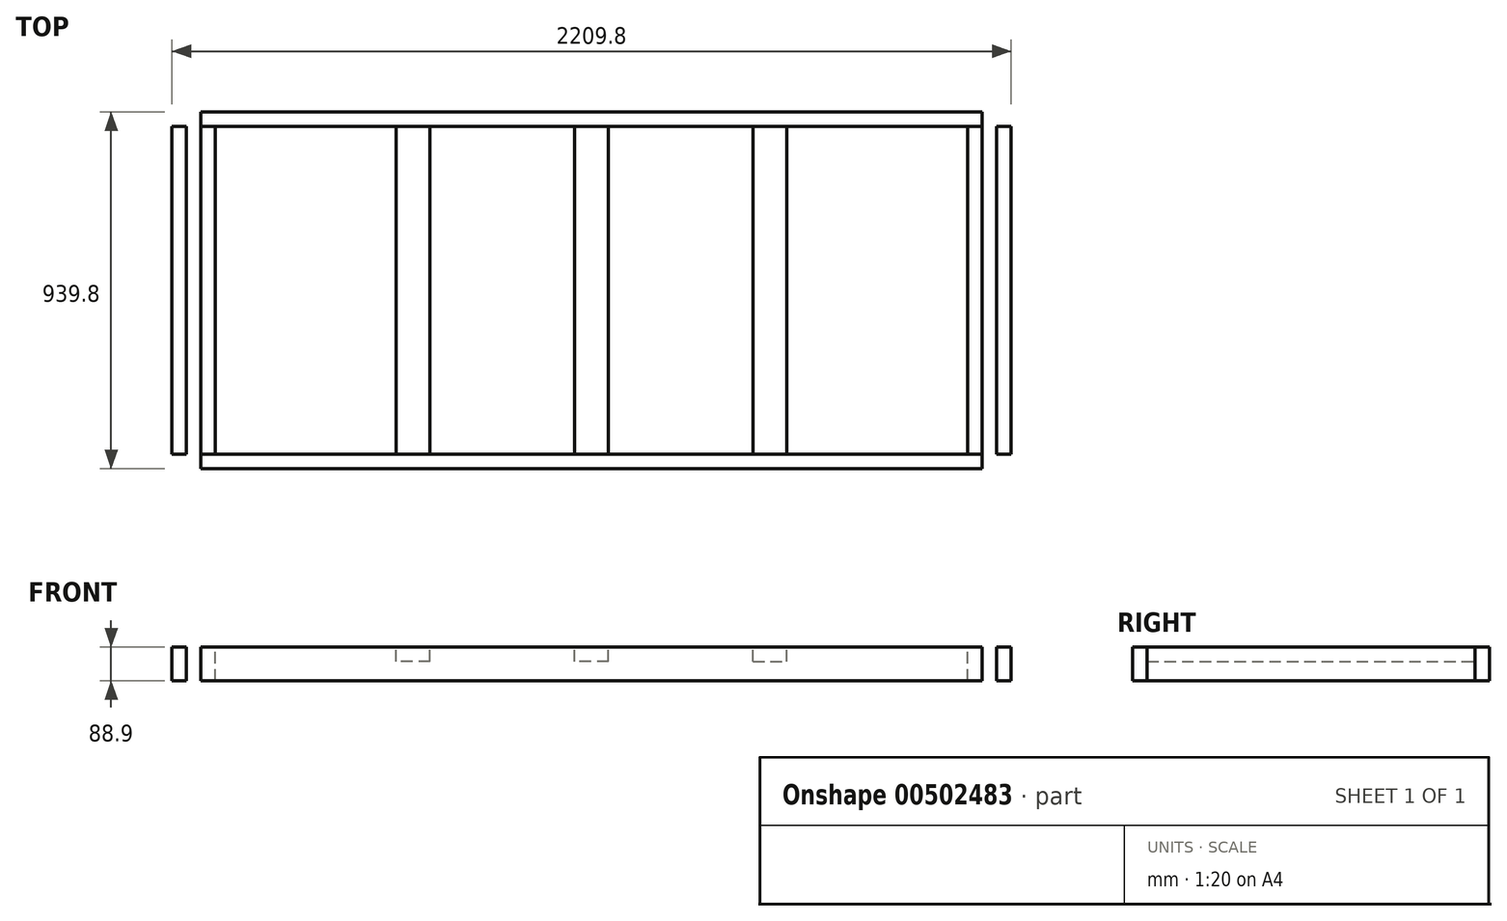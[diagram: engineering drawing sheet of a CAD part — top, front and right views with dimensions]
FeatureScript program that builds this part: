
annotation { "Feature Type Name" : "Feature", "Feature Type Description" : "" }
export const myFeature = defineFeature(function(context is Context, id is Id, definition is map)
    precondition{}
    {
        {
            var Q0;
            Q0=qCreatedBy(makeId("Top.planeOp"),FACE);
            var sketch = newSketch(context, id + "F0", { "sketchPlane" : qUnion([Q0])});
            skLineSegment(sketch, "E0.bottom", {"start": v(44.45, -431.8) * mm, "end": v(-44.45, -431.8) * mm});
            skLineSegment(sketch, "E0.top", {"start": v(44.45, 431.8) * mm, "end": v(-44.45, 431.8) * mm});
            skLineSegment(sketch, "E0.left", {"start": v(44.45, -431.8) * mm, "end": v(44.45, 431.8) * mm});
            skLineSegment(sketch, "E0.right", {"start": v(-44.45, -431.8) * mm, "end": v(-44.45, 431.8) * mm});
            skPoint(sketch, "E0.middle", {"position": v(0, 0) * mm});
            skSolve(sketch);
        }
        {
            var Q0;
            Q0=qCreatedBy(makeId("Top.planeOp"),FACE);
            var sketch = newSketch(context, id + "F1", { "sketchPlane" : qUnion([Q0])});
            skLineSegment(sketch, "E1", {"start": v(-832.76, 0) * mm, "end": v(832.76, 0) * mm, "construction": true});
            skSolve(sketch);
        }
        {
            var Q0;
            Q0=qCreatedBy(makeId("Top.planeOp"),FACE);
            var sketch = newSketch(context, id + "F2", { "sketchPlane" : qUnion([Q0])});
            skLineSegment(sketch, "E2.bottom", {"start": v(-425.45, -431.8) * mm, "end": v(-514.35, -431.8) * mm});
            skLineSegment(sketch, "E2.top", {"start": v(-425.45, 431.8) * mm, "end": v(-514.35, 431.8) * mm});
            skLineSegment(sketch, "E2.left", {"start": v(-425.45, -431.8) * mm, "end": v(-425.45, 431.8) * mm});
            skLineSegment(sketch, "E2.right", {"start": v(-514.35, -431.8) * mm, "end": v(-514.35, 431.8) * mm});
            skPoint(sketch, "E2.middle", {"position": v(-469.9, 0) * mm});
            skSolve(sketch);
        }
        {
            var Q0;
            Q0=qCreatedBy(makeId("Top.planeOp"),FACE);
            var sketch = newSketch(context, id + "F3", { "sketchPlane" : qUnion([Q0])});
            skLineSegment(sketch, "E3.bottom", {"start": v(425.45, 431.8) * mm, "end": v(514.35, 431.8) * mm});
            skLineSegment(sketch, "E3.top", {"start": v(425.45, -431.8) * mm, "end": v(514.35, -431.8) * mm});
            skLineSegment(sketch, "E3.left", {"start": v(425.45, 431.8) * mm, "end": v(425.45, -431.8) * mm});
            skLineSegment(sketch, "E3.right", {"start": v(514.35, 431.8) * mm, "end": v(514.35, -431.8) * mm});
            skPoint(sketch, "E3.middle", {"position": v(469.9, 0) * mm});
            skSolve(sketch);
        }
        {
            var Q0;
            Q0 = qSketchRegion(id + "F0", true);
            var Q1;
            Q1 = qSketchRegion(id + "F2", true);
            var Q2;
            Q2 = qSketchRegion(id + "F3", true);
            extrude(context, id + "F4", {"entities" : qUnion([Q0, Q1, Q2]), "oppositeDirection" : true, "depth" : 38.1 * mm});
        }
        {
            var Q0;
            Q0=qCreatedBy(makeId("Top.planeOp"),FACE);
            var sketch = newSketch(context, id + "F5", { "sketchPlane" : qUnion([Q0])});
            skLineSegment(sketch, "E4.bottom", {"start": v(-990.6, 431.8) * mm, "end": v(-1028.7, 431.8) * mm});
            skLineSegment(sketch, "E4.top", {"start": v(-990.6, -431.8) * mm, "end": v(-1028.7, -431.8) * mm});
            skLineSegment(sketch, "E4.left", {"start": v(-990.6, 431.8) * mm, "end": v(-990.6, -431.8) * mm});
            skLineSegment(sketch, "E4.right", {"start": v(-1028.7, 431.8) * mm, "end": v(-1028.7, -431.8) * mm});
            skPoint(sketch, "E4.middle", {"position": v(-1009.65, 0) * mm});
            skSolve(sketch);
        }
        {
            var Q0;
            Q0=qCreatedBy(makeId("Top.planeOp"),FACE);
            var sketch = newSketch(context, id + "F6", { "sketchPlane" : qUnion([Q0])});
            skLineSegment(sketch, "E5.bottom", {"start": v(-1066.8, 431.8) * mm, "end": v(-1104.9, 431.8) * mm});
            skLineSegment(sketch, "E5.top", {"start": v(-1066.8, -431.8) * mm, "end": v(-1104.9, -431.8) * mm});
            skLineSegment(sketch, "E5.left", {"start": v(-1066.8, 431.8) * mm, "end": v(-1066.8, -431.8) * mm});
            skLineSegment(sketch, "E5.right", {"start": v(-1104.9, 431.8) * mm, "end": v(-1104.9, -431.8) * mm});
            skPoint(sketch, "E5.middle", {"position": v(-1085.85, 0) * mm});
            skSolve(sketch);
        }
        {
            var Q0;
            Q0=qCreatedBy(makeId("Top.planeOp"),FACE);
            var sketch = newSketch(context, id + "F7", { "sketchPlane" : qUnion([Q0])});
            skLineSegment(sketch, "E6.bottom", {"start": v(990.6, 431.8) * mm, "end": v(1028.7, 431.8) * mm});
            skLineSegment(sketch, "E6.top", {"start": v(990.6, -431.8) * mm, "end": v(1028.7, -431.8) * mm});
            skLineSegment(sketch, "E6.left", {"start": v(990.6, 431.8) * mm, "end": v(990.6, -431.8) * mm});
            skLineSegment(sketch, "E6.right", {"start": v(1028.7, 431.8) * mm, "end": v(1028.7, -431.8) * mm});
            skPoint(sketch, "E6.middle", {"position": v(1009.65, 0) * mm});
            skSolve(sketch);
        }
        {
            var Q0;
            Q0=qCreatedBy(makeId("Top.planeOp"),FACE);
            var sketch = newSketch(context, id + "F8", { "sketchPlane" : qUnion([Q0])});
            skLineSegment(sketch, "E7.bottom", {"start": v(1066.8, 431.8) * mm, "end": v(1104.9, 431.8) * mm});
            skLineSegment(sketch, "E7.top", {"start": v(1066.8, -431.8) * mm, "end": v(1104.9, -431.8) * mm});
            skLineSegment(sketch, "E7.left", {"start": v(1066.8, 431.8) * mm, "end": v(1066.8, -431.8) * mm});
            skLineSegment(sketch, "E7.right", {"start": v(1104.9, 431.8) * mm, "end": v(1104.9, -431.8) * mm});
            skPoint(sketch, "E7.middle", {"position": v(1085.85, 0) * mm});
            skSolve(sketch);
        }
        {
            var Q0;
            Q0=qCreatedBy(makeId("Top.planeOp"),FACE);
            var sketch = newSketch(context, id + "F9", { "sketchPlane" : qUnion([Q0])});
            skLineSegment(sketch, "E8.bottom", {"start": v(-1028.7, 431.8) * mm, "end": v(1028.7, 431.8) * mm});
            skLineSegment(sketch, "E8.top", {"start": v(-1028.7, 469.9) * mm, "end": v(1028.7, 469.9) * mm});
            skLineSegment(sketch, "E8.left", {"start": v(-1028.7, 431.8) * mm, "end": v(-1028.7, 469.9) * mm});
            skLineSegment(sketch, "E8.right", {"start": v(1028.7, 431.8) * mm, "end": v(1028.7, 469.9) * mm});
            skSolve(sketch);
        }
        {
            var Q0;
            Q0=qCreatedBy(makeId("Top.planeOp"),FACE);
            var sketch = newSketch(context, id + "F10", { "sketchPlane" : qUnion([Q0])});
            skLineSegment(sketch, "E9.bottom", {"start": v(-1028.7, -469.9) * mm, "end": v(1028.7, -469.9) * mm});
            skLineSegment(sketch, "E9.top", {"start": v(-1028.7, -431.8) * mm, "end": v(1028.7, -431.8) * mm});
            skLineSegment(sketch, "E9.left", {"start": v(-1028.7, -469.9) * mm, "end": v(-1028.7, -431.8) * mm});
            skLineSegment(sketch, "E9.right", {"start": v(1028.7, -469.9) * mm, "end": v(1028.7, -431.8) * mm});
            skSolve(sketch);
        }
        {
            var Q0;
            Q0 = qSketchRegion(id + "F10", true);
            var Q1;
            Q1 = qSketchRegion(id + "F9", true);
            var Q2;
            Q2 = qSketchRegion(id + "F8", true);
            var Q3;
            Q3 = qSketchRegion(id + "F7", true);
            var Q4;
            Q4 = qSketchRegion(id + "F6", true);
            var Q5;
            Q5 = qSketchRegion(id + "F5", true);
            extrude(context, id + "F11", {"entities" : qUnion([Q0, Q1, Q2, Q3, Q4, Q5]), "oppositeDirection" : true, "depth" : 88.9 * mm});
        }
    });
